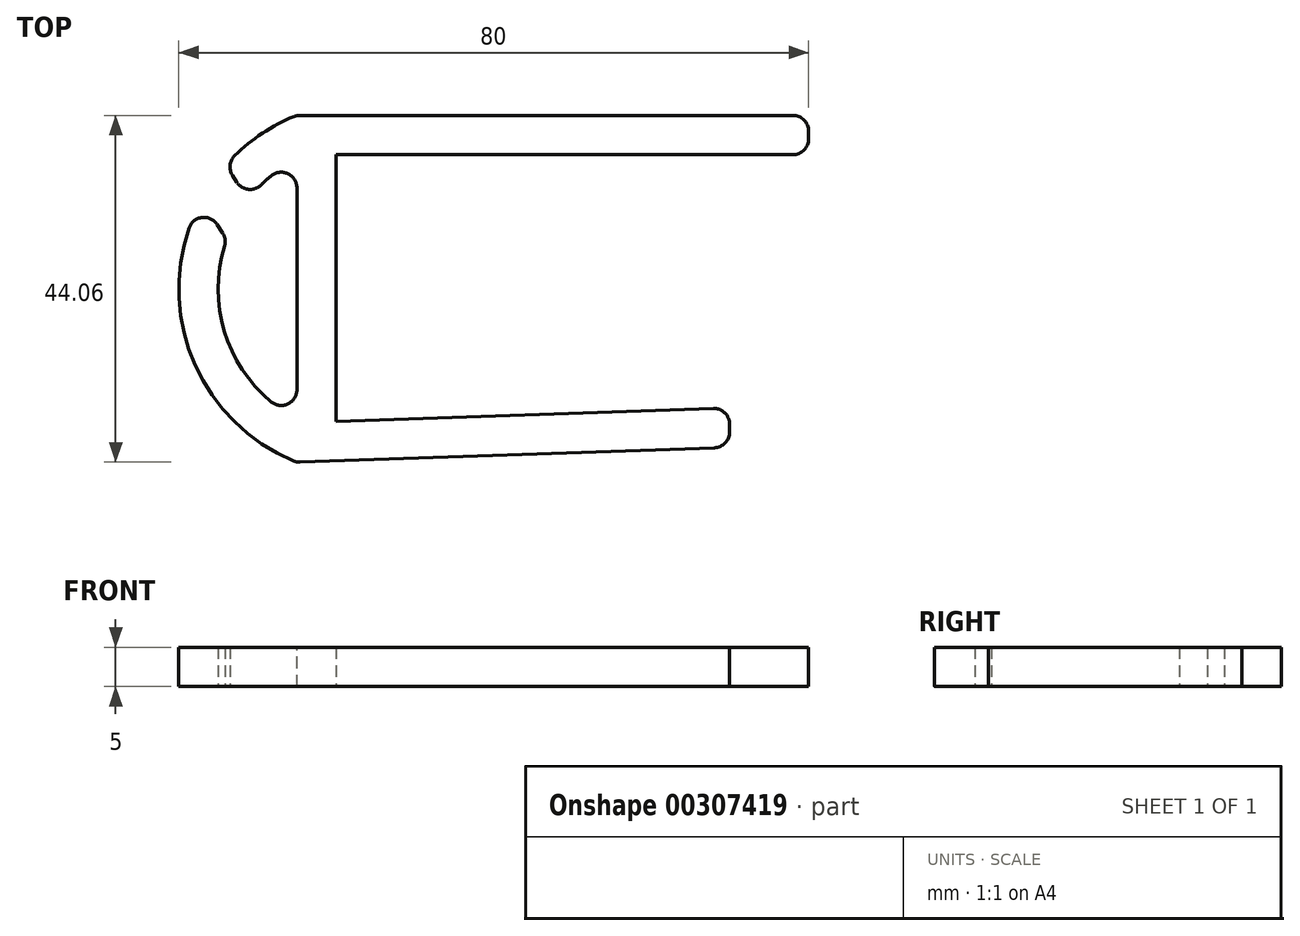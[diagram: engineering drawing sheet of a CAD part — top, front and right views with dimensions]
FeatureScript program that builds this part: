
annotation { "Feature Type Name" : "Feature", "Feature Type Description" : "" }
export const myFeature = defineFeature(function(context is Context, id is Id, definition is map)
    precondition{}
    {
        {
            var Q0;
            Q0=qCreatedBy(makeId("Top.planeOp"),FACE);
            var sketch = newSketch(context, id + "F0", { "sketchPlane" : qUnion([Q0])});
            skLineSegment(sketch, "E0", {"start": v(0, 0) * mm, "end": v(49.97, 1.74) * mm});
            skLineSegment(sketch, "E1", {"start": v(0, 0) * mm, "end": v(0, 33.9) * mm});
            skLineSegment(sketch, "E2", {"start": v(0, 33.9) * mm, "end": v(60, 33.9) * mm});
            skLineSegment(sketch, "E3", {"start": v(49.97, 1.74) * mm, "end": v(49.97, -3.26) * mm});
            skLineSegment(sketch, "E4", {"start": v(49.97, -3.26) * mm, "end": v(-5, -5.18) * mm});
            skLineSegment(sketch, "E5", {"start": v(-5, -5.18) * mm, "end": v(-5, 38.9) * mm});
            skLineSegment(sketch, "E6", {"start": v(-5, 38.9) * mm, "end": v(60, 38.9) * mm});
            skLineSegment(sketch, "E7", {"start": v(60, 38.9) * mm, "end": v(60, 33.9) * mm});
            skArc(sketch, "E8", {"start": v(-5, 38.9) * mm, "mid": v(-20, 16.86) * mm, "end": v(-5, -5.18) * mm});
            skArc(sketch, "E9.0", {"start": v(-5, 33.4) * mm, "mid": v(-15, 16.86) * mm, "end": v(-5, 0.31) * mm});
            skLineSegment(sketch, "E10", {"start": v(-17.13, 28.16) * mm, "end": v(-13.91, 23.14) * mm});
            skLineSegment(sketch, "E11", {"start": v(-14.03, 32.59) * mm, "end": v(-11.2, 28.16) * mm});
            skSolve(sketch);
        }
        {
            var Q0;
            Q0=makeQuery(id+"F0.imprint","IMPRINT",FACE,{"disambiguationData":[TD([[makeQuery(id+"F0.imprint","IMPRINT",EDGE,{"derivedFrom":sQuery(id+"F0.wireOp",EDGE,"E0")}),-1.0]])]});
            var Q1;
            {var subQ5=sQuery(id+"F0.wireOp",EDGE,"E11");Q1=makeQuery(id+"F0.imprint","IMPRINT",FACE,{"disambiguationData":[TD([[makeQuery(id+"F0.imprint","IMPRINT",EDGE,{"derivedFrom":subQ5}),1.0]])]});}
            var Q2;
            {var subQ5=sQuery(id+"F0.wireOp",EDGE,"E10");Q2=makeQuery(id+"F0.imprint","IMPRINT",FACE,{"disambiguationData":[TD([[makeQuery(id+"F0.imprint","IMPRINT",EDGE,{"derivedFrom":subQ5}),-1.0]])]});}
            extrude(context, id + "F1", {"entities" : qUnion([Q0, Q1, Q2]), "depth" : 5 * mm});
        }
        {
            var Q0;
            Q0=makeQuery(id+"F1.opExtrude","SWEPT_EDGE",EDGE,{"disambiguationData":[OSD([sQuery(id+"F0.wireOp",EDGE,"E0"),sQuery(id+"F0.wireOp",EDGE,"E3")])]});
            var Q1;
            Q1=makeQuery(id+"F1.opExtrude","SWEPT_EDGE",EDGE,{"disambiguationData":[OSD([sQuery(id+"F0.wireOp",EDGE,"E3"),sQuery(id+"F0.wireOp",EDGE,"E4")])]});
            var Q2;
            Q2=makeQuery(id+"F1.opExtrude","SWEPT_EDGE",EDGE,{"disambiguationData":[OSD([sQuery(id+"F0.wireOp",EDGE,"E4"),sQuery(id+"F0.wireOp",EDGE,"E5")])]});
            var Q3;
            Q3=makeQuery(id+"F1.opExtrude","SWEPT_EDGE",EDGE,{"disambiguationData":[OSD([sQuery(id+"F0.wireOp",EDGE,"E5"),sQuery(id+"F0.wireOp",EDGE,"tDZMahvT-Mk9m-c3VG-pQvi-6nOqlXWhxI6G")])]});
            var Q4;
            Q4=makeQuery(id+"F1.opExtrude","SWEPT_EDGE",EDGE,{"disambiguationData":[OSD([sQuery(id+"F0.wireOp",EDGE,"E2"),sQuery(id+"F0.wireOp",EDGE,"E7")])]});
            var Q5;
            Q5=makeQuery(id+"F1.opExtrude","SWEPT_EDGE",EDGE,{"disambiguationData":[OSD([sQuery(id+"F0.wireOp",EDGE,"E7"),sQuery(id+"F0.wireOp",EDGE,"ddy3dmFD-jPQb-6u9S-Pvcd-KfanybuG0j5e")])]});
            var Q6;
            Q6=makeQuery(id+"F1.opExtrude","SWEPT_EDGE",EDGE,{"disambiguationData":[OSD([sQuery(id+"F0.wireOp",EDGE,"E8"),sQuery(id+"F0.wireOp",EDGE,"E10")])]});
            var Q7;
            Q7=makeQuery(id+"F1.opExtrude","SWEPT_EDGE",EDGE,{"disambiguationData":[OSD([sQuery(id+"F0.wireOp",EDGE,"E8"),sQuery(id+"F0.wireOp",EDGE,"E11")])]});
            var Q8;
            Q8=makeQuery(id+"F1.opExtrude","SWEPT_EDGE",EDGE,{"disambiguationData":[OSD([sQuery(id+"F0.wireOp",EDGE,"E9.0"),sQuery(id+"F0.wireOp",EDGE,"E10")])]});
            var Q9;
            Q9=makeQuery(id+"F1.opExtrude","SWEPT_EDGE",EDGE,{"disambiguationData":[OSD([sQuery(id+"F0.wireOp",EDGE,"E9.0"),sQuery(id+"F0.wireOp",EDGE,"E11")])]});
            var Q10;
            Q10=makeQuery(id+"F1.opExtrude","SWEPT_EDGE",EDGE,{"disambiguationData":[OSD([sQuery(id+"F0.wireOp",EDGE,"E5"),sQuery(id+"F0.wireOp",EDGE,"E6"),sQuery(id+"F0.wireOp",EDGE,"E8")])]});
            fillet(context, id + "F2", {"entities" : qUnion([Q0, Q1, Q2, Q3, Q4, Q5, Q6, Q7, Q8, Q9, Q10]), "radius" : 2 * mm, "tangentPropagation" : true, "allowEdgeOverflow" : false});
        }
    });
